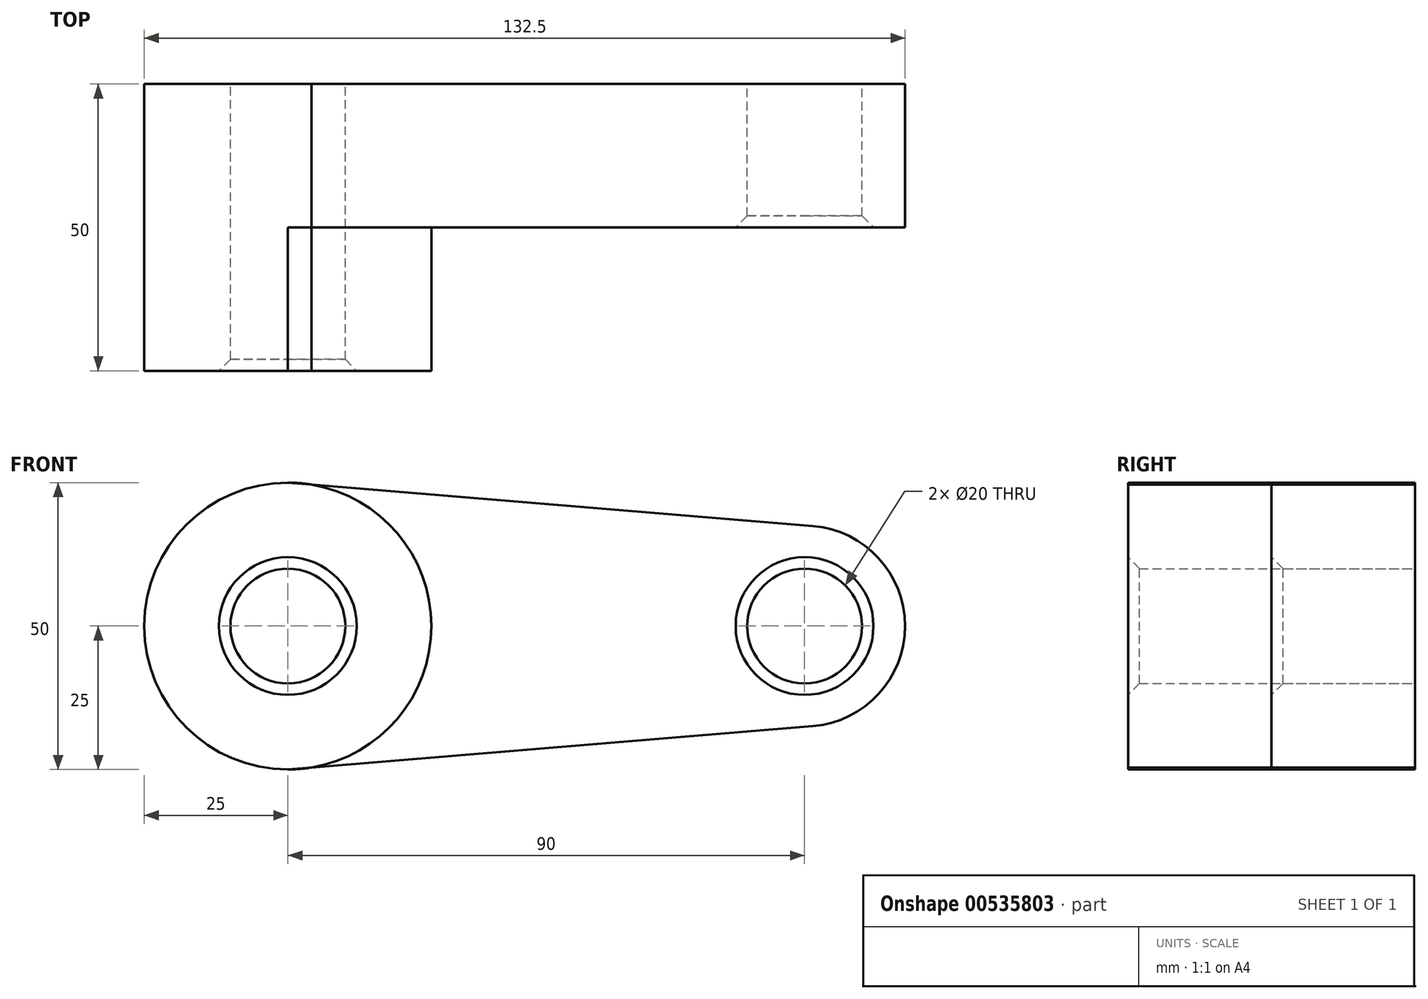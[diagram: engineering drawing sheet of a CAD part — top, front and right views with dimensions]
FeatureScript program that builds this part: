
annotation { "Feature Type Name" : "Feature", "Feature Type Description" : "" }
export const myFeature = defineFeature(function(context is Context, id is Id, definition is map)
    precondition{}
    {
        {
            var Q0;
            Q0=qCreatedBy(makeId("Front.planeOp"),FACE);
            var sketch = newSketch(context, id + "F0", { "sketchPlane" : qUnion([Q0])});
            skCircle(sketch, "E0", {"center": v(0, 0) * mm, "radius": 25 * mm});
            skCircle(sketch, "E1", {"center": v(90, 0) * mm, "radius": 17.5 * mm});
            skLineSegment(sketch, "E2", {"start": v(0, -25) * mm, "end": v(91.44, -17.44) * mm});
            skLineSegment(sketch, "E3", {"start": v(0, 25) * mm, "end": v(91.44, 17.44) * mm});
            skCircle(sketch, "E4", {"center": v(0, 0) * mm, "radius": 10 * mm});
            skCircle(sketch, "E5", {"center": v(90, 0) * mm, "radius": 10 * mm});
            skSolve(sketch);
        }
        {
            var Q0;
            Q0 = qSketchRegion(id + "F0", true);
            extrude(context, id + "F1", {"entities" : qUnion([Q0]), "depth" : 25 * mm, "offsetDistance" : 25 * mm});
        }
        {
            var Q0;
            Q0=makeQuery(id+"F0.imprint","IMPRINT",FACE,{"disambiguationData":[TD([[makeQuery(id+"F0.imprint","IMPRINT",EDGE,{"derivedFrom":sQuery(id+"F0.wireOp",EDGE,"E4")}),-1.0]])]});
            extrude(context, id + "F2", {"entities" : qUnion([Q0]), "operationType" : NewBodyOperationType.ADD, "depth" : 50 * mm, "offsetDistance" : 25 * mm});
        }
        {
            var Q0;
            {var subQ0=sQuery(id+"F0.wireOp",EDGE,"E0");Q0=makeQuery(id+"F2.opExtrude","CAP_EDGE",EDGE,{"disambiguationData":[OSD([subQ0]),TDD([makeQuery(id+"F0.imprint","IMPRINT",EDGE,{"disambiguationData":[TD([[makeQuery(id+"F0.imprint","INTERSECT",VERTEX,{"disambiguationData":[OD(1.0)],"derivedFrom":[subQ0,sQuery(id+"F0.wireOp",EDGE,"E3")]}),1.0]])],"derivedFrom":subQ0})])],"isStart":false});}
            var Q1;
            Q1=makeQuery(id+"F2.opExtrude","CAP_EDGE",EDGE,{"disambiguationData":[OSD([sQuery(id+"F0.wireOp",EDGE,"E4")])],"isStart":false});
            var Q2;
            Q2=makeQuery(id+"F1.opExtrude","CAP_EDGE",EDGE,{"disambiguationData":[OSD([sQuery(id+"F0.wireOp",EDGE,"E5")])],"isStart":false});
            chamfer(context, id + "F3", {"entities" : qUnion([Q0, Q1, Q2]), "width" : 2 * mm, "tangentPropagation" : true});
        }
    });
